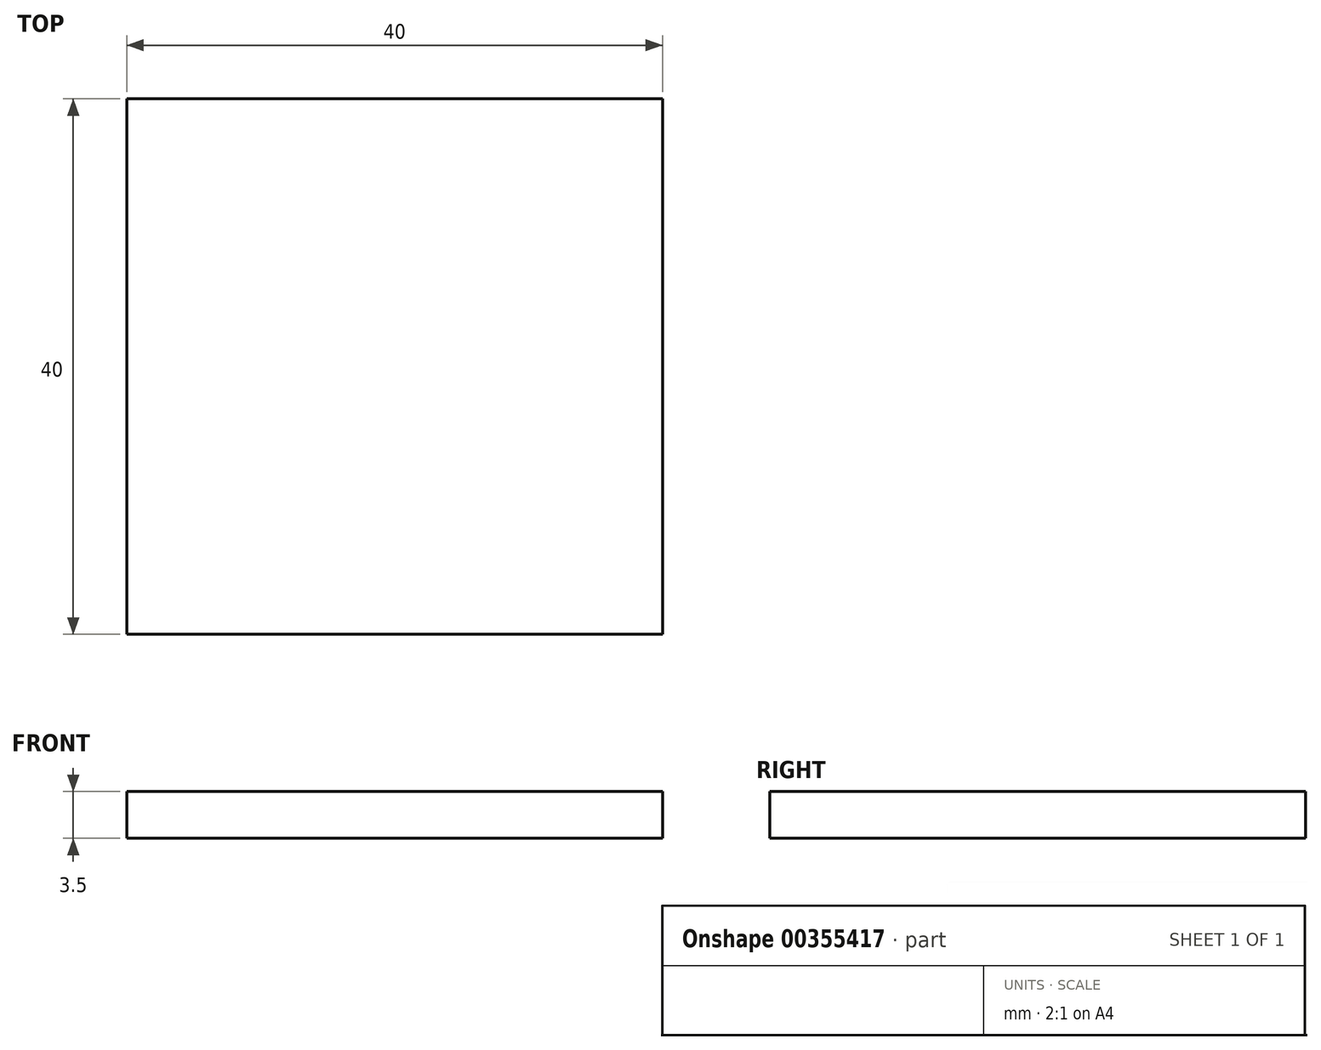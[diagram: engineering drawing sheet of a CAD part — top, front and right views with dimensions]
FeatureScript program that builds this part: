
annotation { "Feature Type Name" : "Feature", "Feature Type Description" : "" }
export const myFeature = defineFeature(function(context is Context, id is Id, definition is map)
    precondition{}
    {
        {
            var Q0;
            Q0=qCreatedBy(makeId("Front.planeOp"),FACE);
            var sketch = newSketch(context, id + "F0", { "sketchPlane" : qUnion([Q0])});
            skLineSegment(sketch, "E0.bottom", {"start": v(-19.4, 1.71) * mm, "end": v(20.6, 1.71) * mm});
            skLineSegment(sketch, "E0.top", {"start": v(-19.4, -1.79) * mm, "end": v(20.6, -1.79) * mm});
            skLineSegment(sketch, "E0.left", {"start": v(-19.4, 1.71) * mm, "end": v(-19.4, -1.79) * mm});
            skLineSegment(sketch, "E0.right", {"start": v(20.6, 1.71) * mm, "end": v(20.6, -1.79) * mm});
            skSolve(sketch);
        }
        {
            var Q0;
            Q0=makeQuery(id+"F0.imprint","IMPRINT",FACE,{"disambiguationData":[TD([[makeQuery(id+"F0.imprint","IMPRINT",EDGE,{"derivedFrom":sQuery(id+"F0.wireOp",EDGE,"E0.bottom")}),-1.0]])]});
            extrude(context, id + "F1", {"entities" : qUnion([Q0]), "depth" : 40 * mm});
        }
    });
